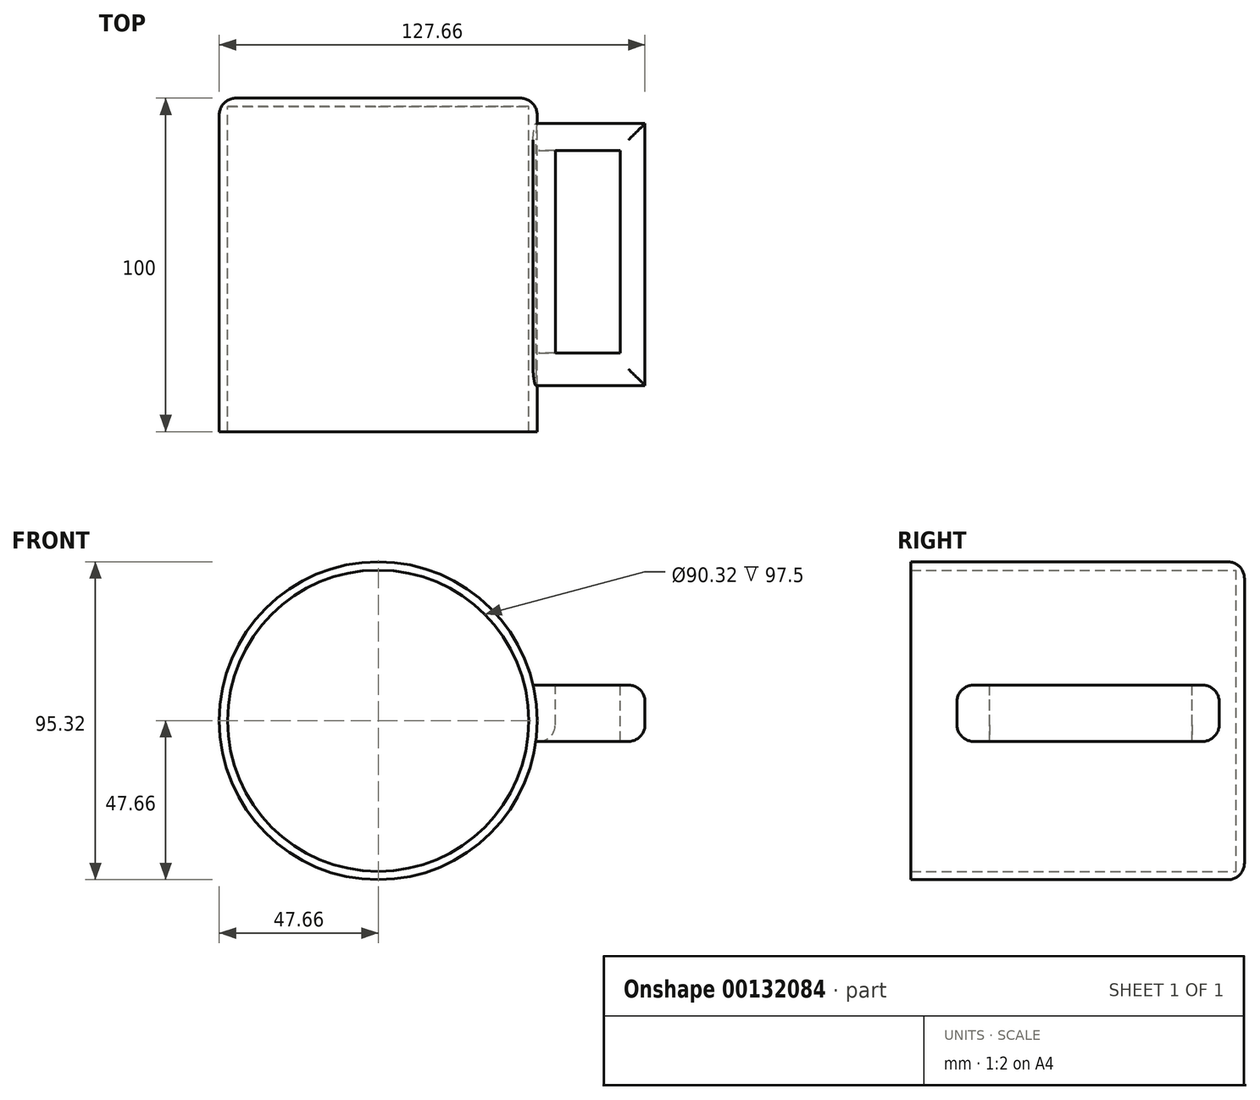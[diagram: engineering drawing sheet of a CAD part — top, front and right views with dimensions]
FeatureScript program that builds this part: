
annotation { "Feature Type Name" : "Feature", "Feature Type Description" : "" }
export const myFeature = defineFeature(function(context is Context, id is Id, definition is map)
    precondition{}
    {
        {
            var Q0;
            Q0=qCreatedBy(makeId("Front.planeOp"),FACE);
            var sketch = newSketch(context, id + "F0", { "sketchPlane" : qUnion([Q0])});
            skCircle(sketch, "E0", {"center": v(0, 0) * mm, "radius": 47.66 * mm});
            skSolve(sketch);
        }
        {
            var Q0;
            Q0=makeQuery(id+"F0.imprint","IMPRINT",FACE,{"disambiguationData":[TD([[makeQuery(id+"F0.imprint","IMPRINT",EDGE,{"derivedFrom":sQuery(id+"F0.wireOp",EDGE,"E0")}),1.0]])]});
            extrude(context, id + "F1", {"entities" : qUnion([Q0]), "depth" : 100 * mm});
        }
        {
            var Q0;
            Q0=makeQuery(id+"F1.opExtrude","CAP_FACE",FACE,{"disambiguationData":[OSD([sQuery(id+"F0.wireOp",EDGE,"E0")])],"isStart":false});
            shell(context, id + "F2", {"entities" : qUnion([Q0]), "thickness" : 2.5 * mm});
        }
        {
            var Q0;
            Q0=qCreatedBy(makeId("Right.planeOp"),FACE);
            cPlane(context, id + "F3", {"entities" : qUnion([Q0]), "cplaneType" : CPlaneType.OFFSET, "offset" : 80 * mm, "width" : 150 * mm, "height" : 150 * mm});
        }
        {
            var Q0;
            Q0=qCreatedBy(id+"F3.planeOp",FACE);
            var sketch = newSketch(context, id + "F4", { "sketchPlane" : qUnion([Q0])});
            skLineSegment(sketch, "E1.bottom", {"start": v(-86.18, -6.2) * mm, "end": v(-7.57, -6.2) * mm});
            skLineSegment(sketch, "E1.top", {"start": v(-86.18, 10.71) * mm, "end": v(-7.57, 10.71) * mm});
            skLineSegment(sketch, "E1.left", {"start": v(-86.18, -6.2) * mm, "end": v(-86.18, 10.71) * mm});
            skLineSegment(sketch, "E1.right", {"start": v(-7.57, -6.2) * mm, "end": v(-7.57, 10.71) * mm});
            skSolve(sketch);
        }
        {
            var Q0;
            Q0 = qSketchRegion(id + "F4", true);
            var Q1;
            Q1=makeQuery(id+"F1.opExtrude","SWEPT_FACE",FACE,{"disambiguationData":[OSD([sQuery(id+"F0.wireOp",EDGE,"E0")])]});
            extrude(context, id + "F5", {"entities" : qUnion([Q0]), "endBound" : BoundingType.UP_TO_SURFACE, "oppositeDirection" : true, "endBoundEntityFace" : qUnion([Q1]), "depth" : 25 * mm});
        }
        {
            var Q0;
            Q0=makeQuery(id+"F5.opExtrude","SWEPT_FACE",FACE,{"disambiguationData":[OSD([sQuery(id+"F4.wireOp",EDGE,"E1.top")])]});
            var sketch = newSketch(context, id + "F6", { "sketchPlane" : qUnion([Q0])});
            skLineSegment(sketch, "E2.bottom", {"start": v(72.52, -76.41) * mm, "end": v(53.08, -76.41) * mm});
            skLineSegment(sketch, "E2.top", {"start": v(72.52, -15.65) * mm, "end": v(53.08, -15.65) * mm});
            skLineSegment(sketch, "E2.left", {"start": v(72.52, -76.41) * mm, "end": v(72.52, -15.65) * mm});
            skLineSegment(sketch, "E2.right", {"start": v(53.08, -76.41) * mm, "end": v(53.08, -15.65) * mm});
            skSolve(sketch);
        }
        {
            var Q0;
            Q0=makeQuery(id+"F6.imprint","IMPRINT",FACE,{"disambiguationData":[TD([[makeQuery(id+"F6.imprint","IMPRINT",EDGE,{"derivedFrom":sQuery(id+"F6.wireOp",EDGE,"E2.bottom")}),-1.0]])]});
            extrude(context, id + "F7", {"entities" : qUnion([Q0]), "operationType" : NewBodyOperationType.REMOVE, "oppositeDirection" : true, "depth" : 25 * mm});
        }
        {
            var Q0;
            Q0=makeQuery(id+"F5.opExtrude","SWEPT_EDGE",EDGE,{"disambiguationData":[OSD([sQuery(id+"F4.wireOp",EDGE,"E1.bottom"),sQuery(id+"F4.wireOp",EDGE,"E1.left")])]});
            var Q1;
            Q1=makeQuery(id+"F5.opExtrude","SWEPT_EDGE",EDGE,{"disambiguationData":[OSD([sQuery(id+"F4.wireOp",EDGE,"E1.top"),sQuery(id+"F4.wireOp",EDGE,"E1.left")])]});
            var Q2;
            Q2=makeQuery(id+"F5.opExtrude","SWEPT_EDGE",EDGE,{"disambiguationData":[OSD([sQuery(id+"F4.wireOp",EDGE,"E1.bottom"),sQuery(id+"F4.wireOp",EDGE,"E1.right")])]});
            var Q3;
            Q3=makeQuery(id+"F5.opExtrude","SWEPT_EDGE",EDGE,{"disambiguationData":[OSD([sQuery(id+"F4.wireOp",EDGE,"E1.top"),sQuery(id+"F4.wireOp",EDGE,"E1.right")])]});
            var Q4;
            Q4=makeQuery(id+"F5.opExtrude","CAP_EDGE",EDGE,{"disambiguationData":[OSD([sQuery(id+"F4.wireOp",EDGE,"E1.top")])],"isStart":true});
            var Q5;
            Q5=makeQuery(id+"F5.opExtrude","CAP_EDGE",EDGE,{"disambiguationData":[OSD([sQuery(id+"F4.wireOp",EDGE,"E1.bottom")])],"isStart":true});
            var Q6;
            Q6=makeQuery(id+"F7.boolean.opBoolean","COPY",EDGE,{"derivedFrom":makeQuery(id+"F7.opExtrude","CAP_EDGE",EDGE,{"disambiguationData":[OSD([sQuery(id+"F6.wireOp",EDGE,"E2.right")])],"isStart":true})});
            var Q7;
            Q7=makeQuery(id+"F7.boolean.opBoolean","INTERSECT",EDGE,{"derivedFrom":[makeQuery(id+"F5.opExtrude","SWEPT_FACE",FACE,{"disambiguationData":[OSD([sQuery(id+"F4.wireOp",EDGE,"E1.bottom")])]}),makeQuery(id+"F7.opExtrude","SWEPT_FACE",FACE,{"disambiguationData":[OSD([sQuery(id+"F6.wireOp",EDGE,"E2.right")])]})]});
            var Q8;
            Q8=makeQuery(id+"F7.boolean.opBoolean","COPY",EDGE,{"derivedFrom":makeQuery(id+"F7.opExtrude","CAP_EDGE",EDGE,{"disambiguationData":[OSD([sQuery(id+"F6.wireOp",EDGE,"E2.bottom")])],"isStart":true})});
            fillet(context, id + "F8", {"entities" : qUnion([Q0, Q1, Q2, Q3, Q4, Q5, Q6, Q7, Q8]), "radius" : 5 * mm, "tangentPropagation" : true, "allowEdgeOverflow" : false});
        }
        {
            var Q0;
            Q0=makeQuery(id+"F1.opExtrude","CAP_EDGE",EDGE,{"disambiguationData":[OSD([sQuery(id+"F0.wireOp",EDGE,"E0")])],"isStart":true});
            fillet(context, id + "F9", {"entities" : qUnion([Q0]), "radius" : 5 * mm, "tangentPropagation" : true, "allowEdgeOverflow" : false});
        }
    });
